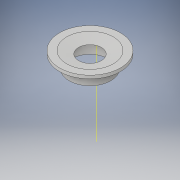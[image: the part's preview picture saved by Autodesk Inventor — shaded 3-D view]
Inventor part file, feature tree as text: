
AUTODESK INVENTOR PART (.ipt)
format: ipt  version: 2017 (Build 210142000, 142)  size: 145,920 bytes
history: native  units: in
note: dims shown in document units (in); Inventor stores cm internally (conversion verified against a paired STEP export)
features: sketch x1, other x1, revolve x1
ambient origin geometry x8: Origin, YZ Plane, XZ Plane, XY Plane, X Axis, Y Axis, Z Axis, Center Point
bodies: Solid1 (feature_tree)
feature tree (3):
  sketch  "Sketch1"  dims[d0=0.25in d2=15.0deg d3=0.1718in d4=0.25in d5=1.5in d6=0.25in d7=0.25in d11=0.125in d15=0.125in d16=0.125in d18=0.375in d20=0.125in d22=0.125in d23=0.1718in d24=0.125in d25=0.5in d26=0.0625in d27=0.0667in d28=0.125in d29=0.125in d30=0.5in d31=0.125in d32=0.5in d33=90.0deg]
  other  "Work Axis1"
  revolve  "Revolution1"  Angle=15.0deg
